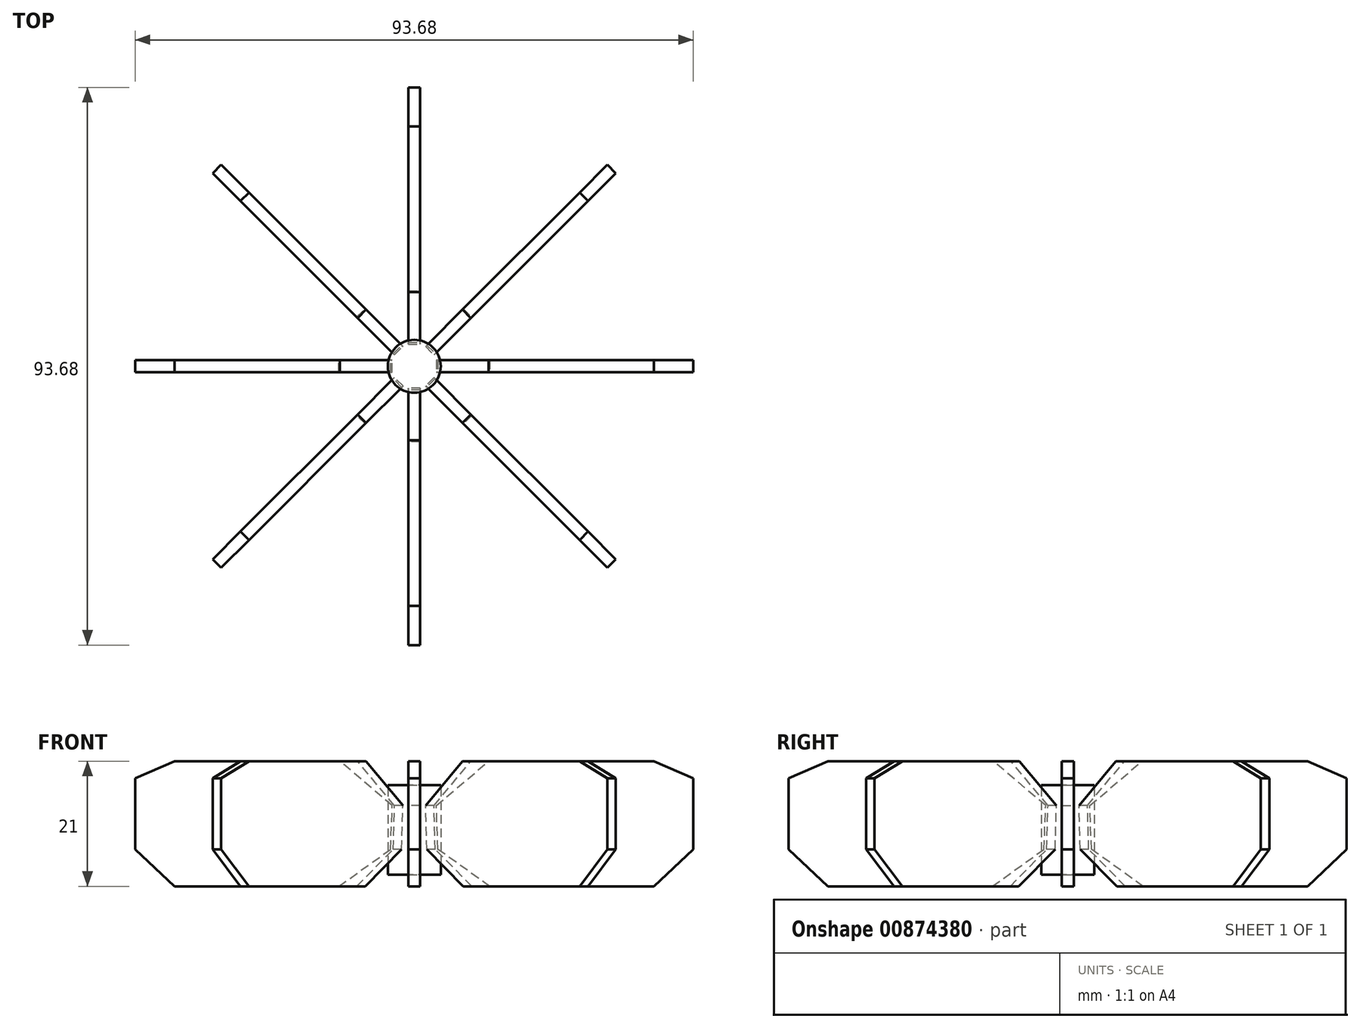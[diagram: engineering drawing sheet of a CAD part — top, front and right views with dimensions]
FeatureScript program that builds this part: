
annotation { "Feature Type Name" : "Feature", "Feature Type Description" : "" }
export const myFeature = defineFeature(function(context is Context, id is Id, definition is map)
    precondition{}
    {
        {
            var Q0;
            Q0=qCreatedBy(makeId("Top.planeOp"),FACE);
            var sketch = newSketch(context, id + "F0", { "sketchPlane" : qUnion([Q0])});
            skCircle(sketch, "E0", {"center": v(0, 0) * mm, "radius": 4.45 * mm});
            skSolve(sketch);
        }
        {
            var Q0;
            Q0=makeQuery(id+"F0.imprint","IMPRINT",FACE,{"disambiguationData":[TD([[makeQuery(id+"F0.imprint","IMPRINT",EDGE,{"derivedFrom":sQuery(id+"F0.wireOp",EDGE,"E0")}),1.0]])]});
            extrude(context, id + "F1", {"entities" : qUnion([Q0]), "endBound" : BoundingType.SYMMETRIC, "depth" : 15 * mm, "offsetDistance" : 25 * mm});
        }
        {
            var Q0;
            Q0=qCreatedBy(makeId("Right.planeOp"),FACE);
            var sketch = newSketch(context, id + "F2", { "sketchPlane" : qUnion([Q0])});
            skLineSegment(sketch, "E1", {"start": v(-3.7, 4.07) * mm, "end": v(-12.46, 11.53) * mm});
            skLineSegment(sketch, "E2", {"start": v(-12.46, 11.53) * mm, "end": v(-40.25, 11.53) * mm});
            skLineSegment(sketch, "E3", {"start": v(-40.25, 11.53) * mm, "end": v(-46.84, 8.65) * mm});
            skLineSegment(sketch, "E4", {"start": v(-46.84, 8.65) * mm, "end": v(-46.84, -3.27) * mm});
            skLineSegment(sketch, "E5", {"start": v(-46.84, -3.27) * mm, "end": v(-40.25, -9.47) * mm});
            skLineSegment(sketch, "E6", {"start": v(-40.25, -9.47) * mm, "end": v(-12.66, -9.47) * mm});
            skLineSegment(sketch, "E7", {"start": v(-12.66, -9.47) * mm, "end": v(-3.98, -3.27) * mm});
            skLineSegment(sketch, "E8", {"start": v(-3.98, -3.27) * mm, "end": v(-3.7, 4.07) * mm});
            skSolve(sketch);
        }
        {
            var Q0;
            Q0=makeQuery(id+"F2.imprint","IMPRINT",FACE,{"disambiguationData":[TD([[makeQuery(id+"F2.imprint","IMPRINT",EDGE,{"derivedFrom":sQuery(id+"F2.wireOp",EDGE,"E1")}),1.0]])]});
            extrude(context, id + "F3", {"entities" : qUnion([Q0]), "endBound" : BoundingType.SYMMETRIC, "depth" : 2 * mm, "offsetDistance" : 25 * mm});
        }
        {
            var Q0;
            Q0=makeQuery(id+"F3.opExtrude","SWEPT_BODY",BODY,{"disambiguationData":[OSD([sQuery(id+"F2.wireOp",EDGE,"E1"),sQuery(id+"F2.wireOp",EDGE,"E2"),sQuery(id+"F2.wireOp",EDGE,"E3"),sQuery(id+"F2.wireOp",EDGE,"E4"),sQuery(id+"F2.wireOp",EDGE,"E5"),sQuery(id+"F2.wireOp",EDGE,"E6"),sQuery(id+"F2.wireOp",EDGE,"E7"),sQuery(id+"F2.wireOp",EDGE,"E8")])]});
            var Q1;
            Q1=makeQuery(id+"F1.opExtrude","SWEPT_FACE",FACE,{"disambiguationData":[OSD([sQuery(id+"F0.wireOp",EDGE,"E0")])]});
            circularPattern(context, id + "F4", {"entities" : qUnion([Q0]), "axis" : qUnion([Q1]), "angle" : 360 * degree, "instanceCount" : 8, "equalSpace" : true});
        }
    });
